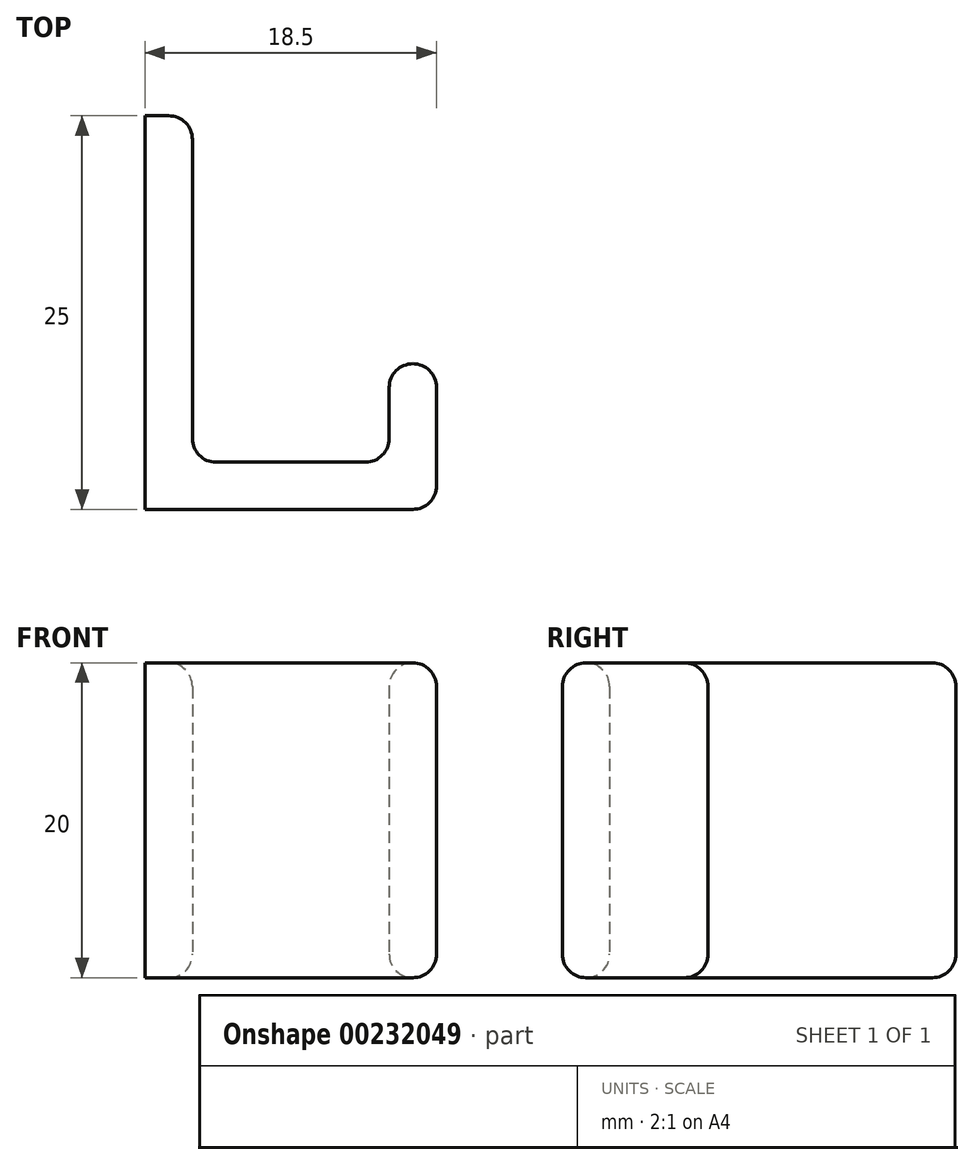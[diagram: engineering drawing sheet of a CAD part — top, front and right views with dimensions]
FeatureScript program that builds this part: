
annotation { "Feature Type Name" : "Feature", "Feature Type Description" : "" }
export const myFeature = defineFeature(function(context is Context, id is Id, definition is map)
    precondition{}
    {
        {
            var Q0;
            Q0=qCreatedBy(makeId("Top.planeOp"),FACE);
            var sketch = newSketch(context, id + "F0", { "sketchPlane" : qUnion([Q0])});
            skLineSegment(sketch, "E0", {"start": v(0, 25) * mm, "end": v(0, 0) * mm});
            skLineSegment(sketch, "E1", {"start": v(0, 0) * mm, "end": v(17, 0) * mm});
            skLineSegment(sketch, "E2", {"start": v(18.5, 1.5) * mm, "end": v(18.5, 7.75) * mm});
            skLineSegment(sketch, "E3", {"start": v(17, 9.25) * mm, "end": v(17, 9.25) * mm});
            skLineSegment(sketch, "E4", {"start": v(15.5, 7.75) * mm, "end": v(15.5, 4.5) * mm});
            skLineSegment(sketch, "E5", {"start": v(14, 3) * mm, "end": v(4.5, 3) * mm});
            skLineSegment(sketch, "E6", {"start": v(3, 4.5) * mm, "end": v(3, 23.5) * mm});
            skLineSegment(sketch, "E7", {"start": v(1.5, 25) * mm, "end": v(0, 25) * mm});
            skPoint(sketch, "E8.visualSharp", {"position": v(3, 25) * mm});
            skArc(sketch, "E8.filletArc", {"start": v(3, 23.5) * mm, "mid": v(2.56, 24.56) * mm, "end": v(1.5, 25) * mm});
            skPoint(sketch, "E9.visualSharp", {"position": v(3, 3) * mm});
            skArc(sketch, "E9.filletArc", {"start": v(3, 4.5) * mm, "mid": v(3.44, 3.44) * mm, "end": v(4.5, 3) * mm});
            skPoint(sketch, "E10.visualSharp", {"position": v(15.5, 3) * mm});
            skArc(sketch, "E10.filletArc", {"start": v(14, 3) * mm, "mid": v(15.06, 3.44) * mm, "end": v(15.5, 4.5) * mm});
            skPoint(sketch, "E11.visualSharp", {"position": v(15.5, 9.25) * mm});
            skArc(sketch, "E11.filletArc", {"start": v(17, 9.25) * mm, "mid": v(15.94, 8.81) * mm, "end": v(15.5, 7.75) * mm});
            skPoint(sketch, "E12.visualSharp", {"position": v(18.5, 0) * mm});
            skArc(sketch, "E12.filletArc", {"start": v(17, 0) * mm, "mid": v(18.06, 0.44) * mm, "end": v(18.5, 1.5) * mm});
            skPoint(sketch, "E13.visualSharp", {"position": v(18.5, 9.25) * mm});
            skArc(sketch, "E13.filletArc", {"start": v(18.5, 7.75) * mm, "mid": v(18.06, 8.81) * mm, "end": v(17, 9.25) * mm});
            skSolve(sketch);
        }
        {
            var Q0;
            Q0 = qSketchRegion(id + "F0", true);
            extrude(context, id + "F1", {"entities" : qUnion([Q0]), "depth" : 20 * mm});
        }
        {
            var Q0;
            Q0=makeQuery(id+"F1.opExtrude","CAP_EDGE",EDGE,{"disambiguationData":[OSD([sQuery(id+"F0.wireOp",EDGE,"E6")])],"isStart":false});
            var Q1;
            Q1=makeQuery(id+"F1.opExtrude","CAP_EDGE",EDGE,{"disambiguationData":[OSD([sQuery(id+"F0.wireOp",EDGE,"E5")])],"isStart":true});
            fillet(context, id + "F2", {"entities" : qUnion([Q0, Q1]), "radius" : 1.5 * mm, "tangentPropagation" : true, "allowEdgeOverflow" : false});
        }
    });
